# Revit family: 1604A_Enclosed10AMP
name_source: partatom
category: Communication Devices
units: mm (PartAtom-declared; Revit-internal decimal feet)

## family parameters
Cut with Voids When Loaded = No
Host = Face
Maintain Annotation Orientation = No
OmniClass Number = 23.85.80.11.27
OmniClass Title = Lighting Controls
Part Type = Normal
Room Calculation Point = No
Round Connector Dimension = Use Diameter
Shared = Yes

## types (1)
- 1604A_Enclosed10AMP
    Assembly Code = D5090
    Certification = UL and cUL Listed
    Default Elevation = 48 "
    Description = nxlightingcontrols RR1SPDTC relays provide an isolated N.O. / N.C. contact that can be used to integrate low voltage sensors to other building automation systems. The coil contained in these relays work off a variety of voltages from low voltage to high voltage. An externally visible LED indicates the status of the coil of the relay.
    Features = 10 Amp SPDT Relay
Available with either 10-30 VAC/DC/120 VAC Coil or 10-30 VAC/DC/208-277 VAC Coil
LED status indicator
N.O. and N.C. isolated contacts
UL and cUL listed
One-year warranty
    Housing Material = Metal-Galvanized_Steel
    L = 1 "
    LED = Paint -  Red
    Manufacturer = NX Lighting Controls
    Model = MP347A Power Pack
    Type Comments = Enclosed 10 Amp SPDT Relays
    URL = https://www.currentlighting.com
    W = 2 "
    Warranty = 5-Years Warranty
    Washer = Paint -  Carbon Black

## geometry (parser evidence)
native form markers: Sweep x3
no freeform markers — native parametric forms only
